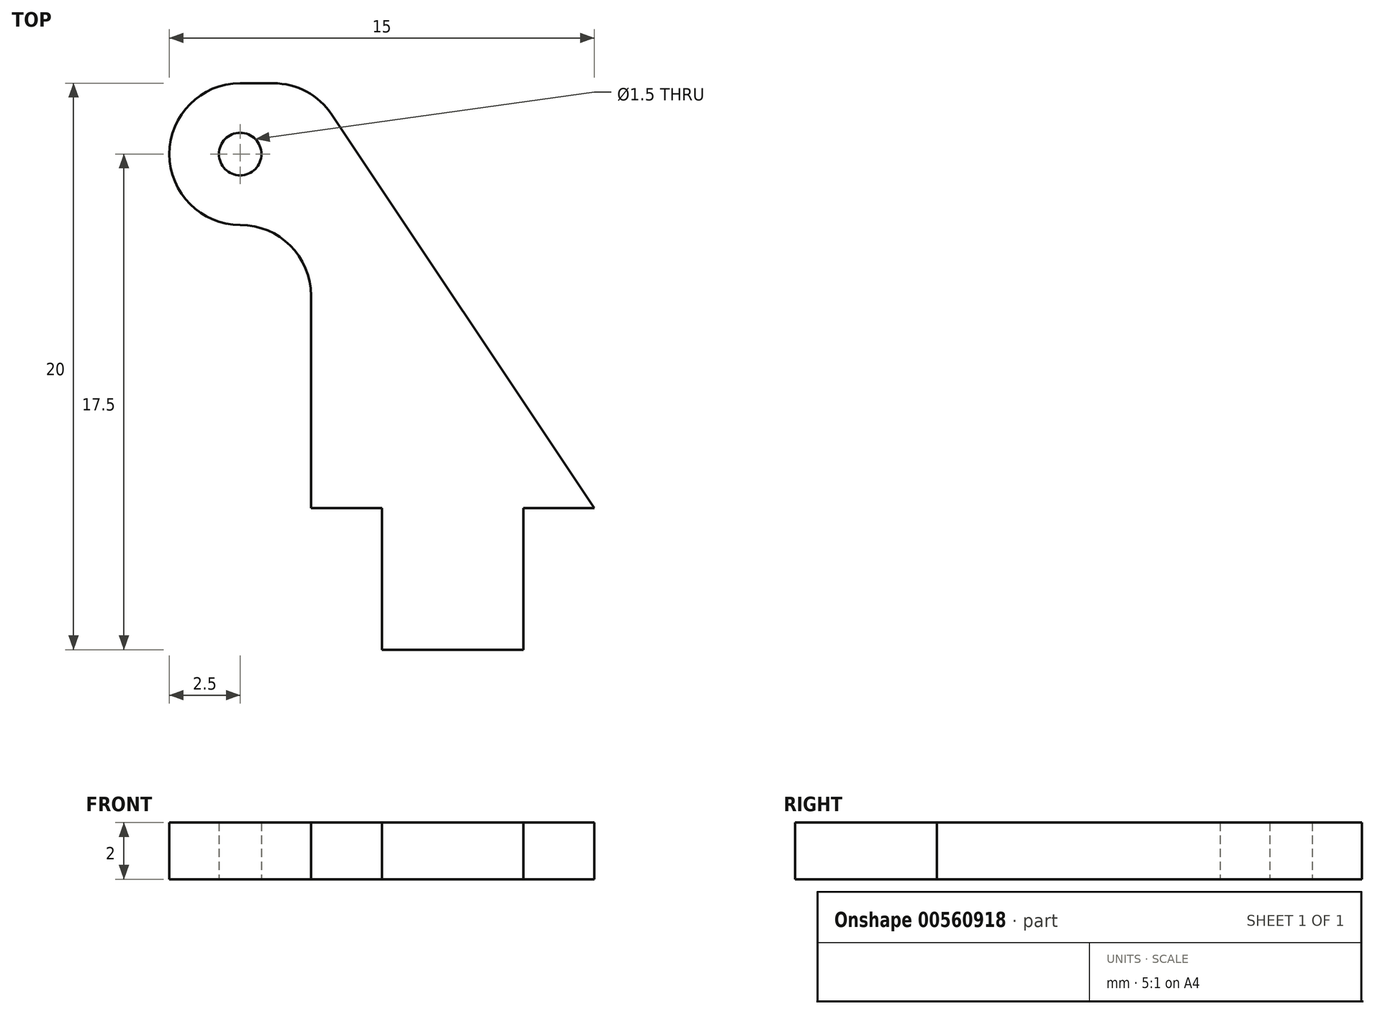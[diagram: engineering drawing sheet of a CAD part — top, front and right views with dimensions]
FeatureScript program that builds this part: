
annotation { "Feature Type Name" : "Feature", "Feature Type Description" : "" }
export const myFeature = defineFeature(function(context is Context, id is Id, definition is map)
    precondition{}
    {
        {
            var Q0;
            Q0=qCreatedBy(makeId("Top.planeOp"),FACE);
            var sketch = newSketch(context, id + "F0", { "sketchPlane" : qUnion([Q0])});
            skLineSegment(sketch, "E0.bottom", {"start": v(-2.5, -5) * mm, "end": v(2.5, -5) * mm});
            skLineSegment(sketch, "E0.top", {"start": v(-2.5, 0) * mm, "end": v(2.5, 0) * mm});
            skLineSegment(sketch, "E0.left", {"start": v(-2.5, -5) * mm, "end": v(-2.5, 0) * mm});
            skLineSegment(sketch, "E0.right", {"start": v(2.5, -5) * mm, "end": v(2.5, 0) * mm});
            skLineSegment(sketch, "E1", {"start": v(-2.5, 0) * mm, "end": v(-5, 0) * mm});
            skLineSegment(sketch, "E2", {"start": v(-5, 0) * mm, "end": v(-5, 10) * mm});
            skLineSegment(sketch, "E3", {"start": v(-5, 10) * mm, "end": v(-10, 10) * mm});
            skLineSegment(sketch, "E4", {"start": v(-10, 10) * mm, "end": v(-10, 15) * mm});
            skLineSegment(sketch, "E5", {"start": v(-10, 15) * mm, "end": v(-5, 15) * mm});
            skLineSegment(sketch, "E6", {"start": v(-5, 15) * mm, "end": v(5, 0) * mm});
            skLineSegment(sketch, "E7", {"start": v(5, 0) * mm, "end": v(2.5, 0) * mm});
            skCircle(sketch, "E8", {"center": v(-7.5, 12.5) * mm, "radius": 0.75 * mm});
            skSolve(sketch);
        }
        {
            var Q0;
            Q0=makeQuery(id+"F0.imprint","IMPRINT",FACE,{"disambiguationData":[TD([[makeQuery(id+"F0.imprint","IMPRINT",EDGE,{"derivedFrom":sQuery(id+"F0.wireOp",EDGE,"E0.top")}),1.0]])]});
            var Q1;
            Q1=makeQuery(id+"F0.imprint","IMPRINT",FACE,{"disambiguationData":[TD([[makeQuery(id+"F0.imprint","IMPRINT",EDGE,{"derivedFrom":sQuery(id+"F0.wireOp",EDGE,"E0.bottom")}),1.0]])]});
            extrude(context, id + "F1", {"entities" : qUnion([Q0, Q1]), "depth" : 2 * mm, "offsetDistance" : 25 * mm});
        }
        {
            var Q0;
            Q0=makeQuery(id+"F1.opExtrude","SWEPT_EDGE",EDGE,{"disambiguationData":[OSD([sQuery(id+"F0.wireOp",EDGE,"E4"),sQuery(id+"F0.wireOp",EDGE,"E5")])]});
            var Q1;
            Q1=makeQuery(id+"F1.opExtrude","SWEPT_EDGE",EDGE,{"disambiguationData":[OSD([sQuery(id+"F0.wireOp",EDGE,"E3"),sQuery(id+"F0.wireOp",EDGE,"E4")])]});
            var Q2;
            Q2=makeQuery(id+"F1.opExtrude","SWEPT_EDGE",EDGE,{"disambiguationData":[OSD([sQuery(id+"F0.wireOp",EDGE,"E5"),sQuery(id+"F0.wireOp",EDGE,"E6")])]});
            var Q3;
            Q3=makeQuery(id+"F1.opExtrude","SWEPT_EDGE",EDGE,{"disambiguationData":[OSD([sQuery(id+"F0.wireOp",EDGE,"E2"),sQuery(id+"F0.wireOp",EDGE,"E3")])]});
            fillet(context, id + "F2", {"entities" : qUnion([Q0, Q1, Q2, Q3]), "radius" : 2.5 * mm, "tangentPropagation" : true, "allowEdgeOverflow" : false});
        }
    });
